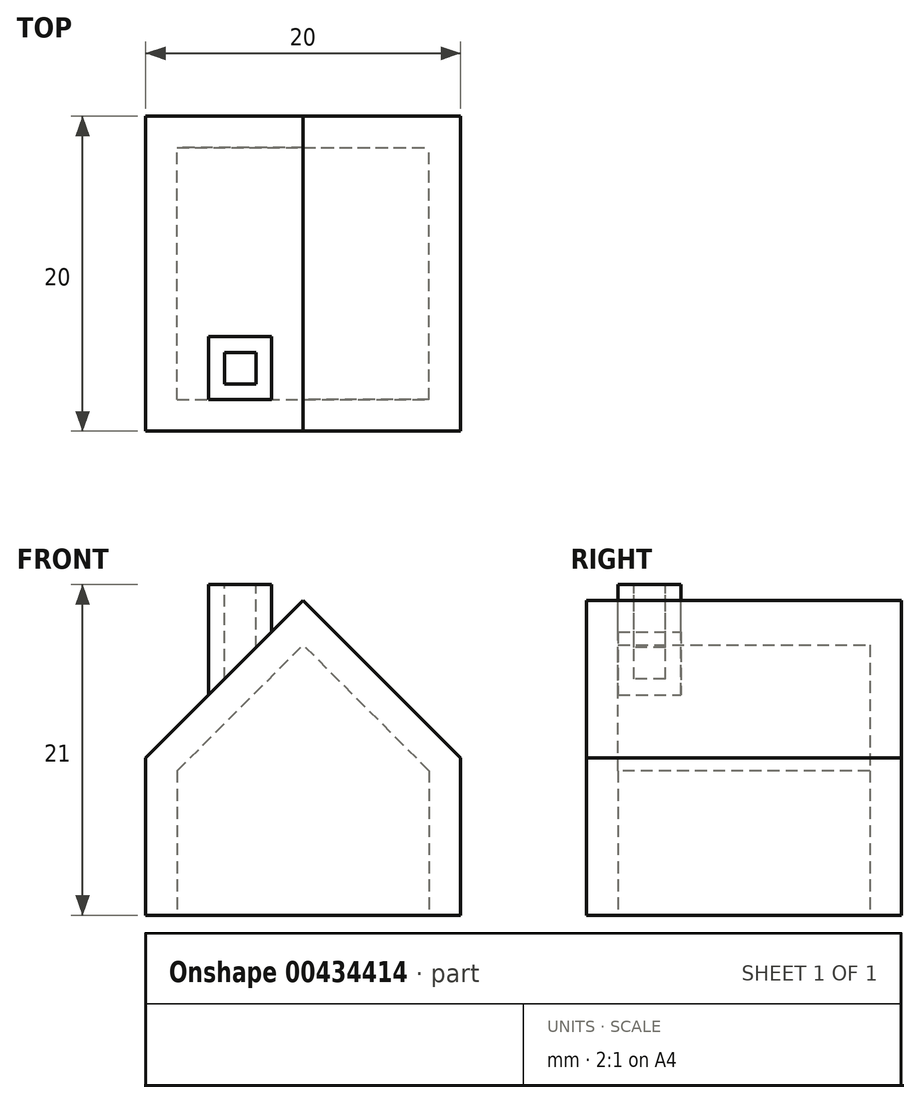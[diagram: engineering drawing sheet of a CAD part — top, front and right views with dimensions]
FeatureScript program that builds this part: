
annotation { "Feature Type Name" : "Feature", "Feature Type Description" : "" }
export const myFeature = defineFeature(function(context is Context, id is Id, definition is map)
    precondition{}
    {
        {
            var Q0;
            Q0=qCreatedBy(makeId("Top.planeOp"),FACE);
            var sketch = newSketch(context, id + "F0", { "sketchPlane" : qUnion([Q0])});
            skLineSegment(sketch, "E0.bottom", {"start": v(0, 0) * mm, "end": v(20, 0) * mm});
            skLineSegment(sketch, "E0.top", {"start": v(0, 20) * mm, "end": v(20, 20) * mm});
            skLineSegment(sketch, "E0.left", {"start": v(0, 0) * mm, "end": v(0, 20) * mm});
            skLineSegment(sketch, "E0.right", {"start": v(20, 0) * mm, "end": v(20, 20) * mm});
            skSolve(sketch);
        }
        {
            var Q0;
            Q0 = qSketchRegion(id + "F0", true);
            extrude(context, id + "F1", {"entities" : qUnion([Q0]), "depth" : 20 * mm});
        }
        {
            var Q0;
            Q0=makeQuery(id+"F1.opExtrude","CAP_EDGE",EDGE,{"disambiguationData":[OSD([sQuery(id+"F0.wireOp",EDGE,"E0.left")])],"isStart":false});
            var Q1;
            Q1=makeQuery(id+"F1.opExtrude","CAP_EDGE",EDGE,{"disambiguationData":[OSD([sQuery(id+"F0.wireOp",EDGE,"E0.right")])],"isStart":false});
            chamfer(context, id + "F2", {"entities" : qUnion([Q0, Q1]), "width" : 10 * mm, "tangentPropagation" : true});
        }
        {
            var Q0;
            Q0=makeQuery(id+"F1.opExtrude","CAP_FACE",FACE,{"disambiguationData":[OSD([sQuery(id+"F0.wireOp",EDGE,"E0.bottom"),sQuery(id+"F0.wireOp",EDGE,"E0.top"),sQuery(id+"F0.wireOp",EDGE,"E0.left"),sQuery(id+"F0.wireOp",EDGE,"E0.right")])],"isStart":true});
            shell(context, id + "F3", {"entities" : qUnion([Q0]), "thickness" : 2 * mm});
        }
        {
            var Q0;
            Q0=makeQuery(id+"F2.opChamfer","BLEND_VERTEX",VERTEX,{"blendedFrom":[makeQuery(id+"F1.opExtrude","CAP_EDGE",EDGE,{"disambiguationData":[OSD([sQuery(id+"F0.wireOp",EDGE,"E0.left")])],"isStart":false}),makeQuery(id+"F1.opExtrude","CAP_EDGE",EDGE,{"disambiguationData":[OSD([sQuery(id+"F0.wireOp",EDGE,"E0.right")])],"isStart":false}),makeQuery(id+"F1.opExtrude","SWEPT_FACE",FACE,{"disambiguationData":[OSD([sQuery(id+"F0.wireOp",EDGE,"E0.bottom")])]})],"blendedInto":[makeQuery(id+"F1.opExtrude","SWEPT_FACE",FACE,{"disambiguationData":[OSD([sQuery(id+"F0.wireOp",EDGE,"E0.bottom")])]})]});
            var Q1;
            Q1=makeQuery(id+"F1.opExtrude","SWEPT_EDGE",EDGE,{"disambiguationData":[OSD([sQuery(id+"F0.wireOp",EDGE,"E0.bottom"),sQuery(id+"F0.wireOp",EDGE,"E0.right")])]});
            cPlane(context, id + "F4", {"entities" : qUnion([Q0, Q1]), "cplaneType" : CPlaneType.LINE_POINT, "offset" : 25 * mm, "width" : 150 * mm, "height" : 150 * mm});
        }
        {
            var Q0;
            Q0=qCreatedBy(id+"F4.planeOp",FACE);
            var sketch = newSketch(context, id + "F5", { "sketchPlane" : qUnion([Q0])});
            skLineSegment(sketch, "E1.bottom", {"start": v(8, -2) * mm, "end": v(4, -2) * mm});
            skLineSegment(sketch, "E1.top", {"start": v(8, -6) * mm, "end": v(4, -6) * mm});
            skLineSegment(sketch, "E1.left", {"start": v(8, -2) * mm, "end": v(8, -6) * mm});
            skLineSegment(sketch, "E1.right", {"start": v(4, -2) * mm, "end": v(4, -6) * mm});
            skLineSegment(sketch, "E2.bottom", {"start": v(8, -2) * mm, "end": v(10, -2) * mm, "construction": true});
            skLineSegment(sketch, "E2.top", {"start": v(8, 0) * mm, "end": v(10, 0) * mm, "construction": true});
            skLineSegment(sketch, "E2.left", {"start": v(8, -2) * mm, "end": v(8, 0) * mm, "construction": true});
            skLineSegment(sketch, "E2.right", {"start": v(10, -2) * mm, "end": v(10, 0) * mm, "construction": true});
            skLineSegment(sketch, "E3.bottom", {"start": v(5, -5) * mm, "end": v(7, -5) * mm});
            skLineSegment(sketch, "E3.top", {"start": v(5, -3) * mm, "end": v(7, -3) * mm});
            skLineSegment(sketch, "E3.left", {"start": v(5, -5) * mm, "end": v(5, -3) * mm});
            skLineSegment(sketch, "E3.right", {"start": v(7, -5) * mm, "end": v(7, -3) * mm});
            skPoint(sketch, "E3.middle", {"position": v(6, -4) * mm});
            skPoint(sketch, "E3.middle.positionSnap0", {"position": v(8, -4) * mm});
            skPoint(sketch, "E3.middle.positionSnap1", {"position": v(6, -2) * mm});
            skPoint(sketch, "E3.centerSnap0", {"position": v(8, -4) * mm});
            skPoint(sketch, "E3.centerSnap1", {"position": v(6, -2) * mm});
            skSolve(sketch);
        }
        {
            var Q0;
            Q0 = qSketchRegion(id + "F5", true);
            var Q1;
            Q1=makeQuery(id+"F2.opChamfer","BLEND_FACE",FACE,{"disambiguationData":[OSD([sQuery(id+"F0.wireOp",EDGE,"E0.left")])]});
            extrude(context, id + "F6", {"entities" : qUnion([Q0]), "operationType" : NewBodyOperationType.ADD, "endBound" : BoundingType.UP_TO_SURFACE, "endBoundEntityFace" : qUnion([Q1]), "depth" : 25 * mm, "hasSecondDirection" : true, "secondDirectionOppositeDirection" : true, "secondDirectionDepth" : 1 * mm});
        }
    });
